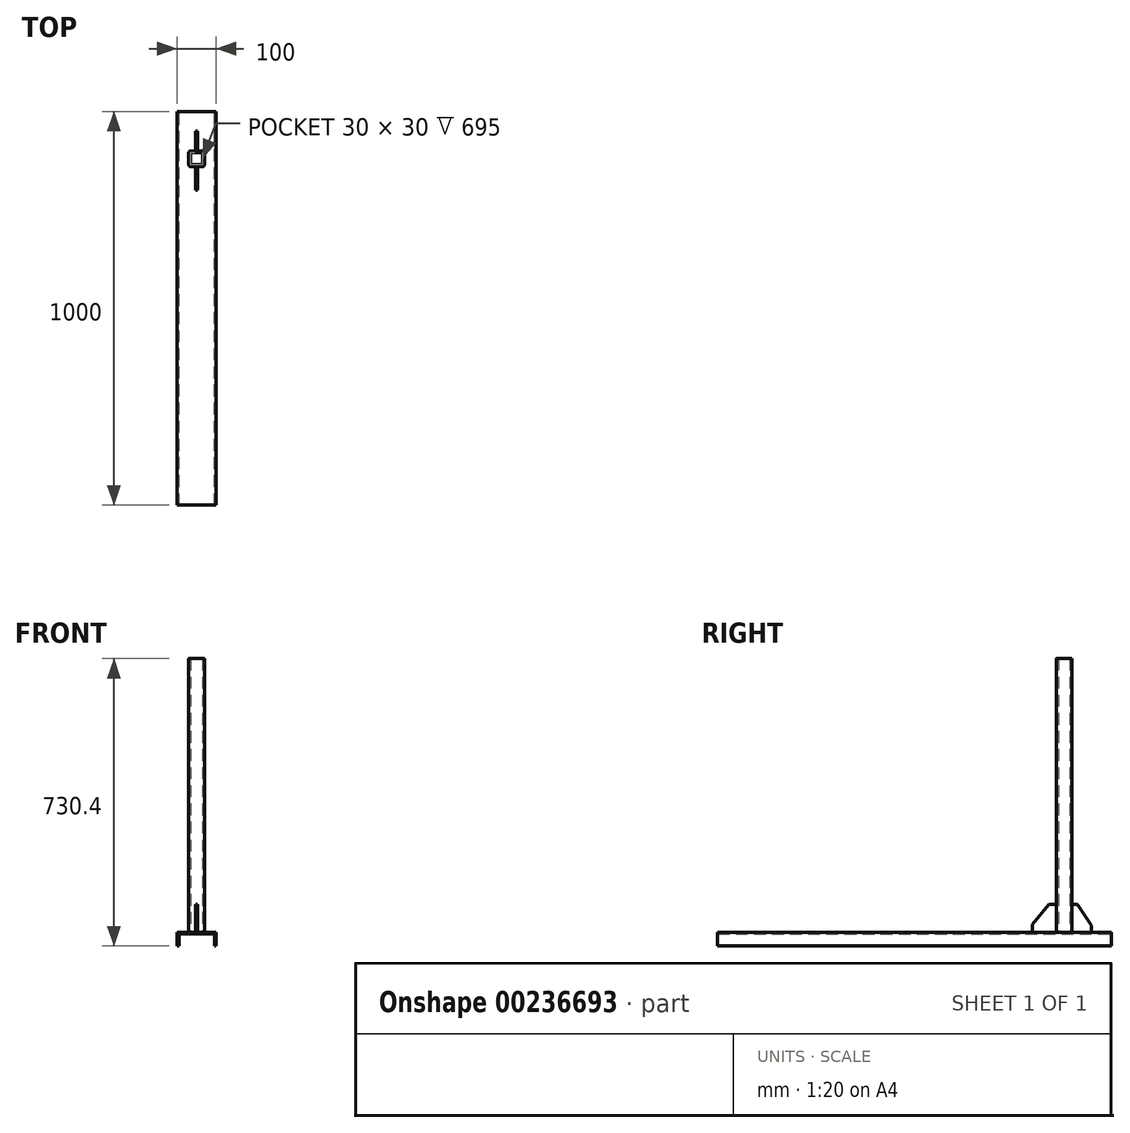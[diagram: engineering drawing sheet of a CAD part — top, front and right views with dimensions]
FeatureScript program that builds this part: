
annotation { "Feature Type Name" : "Feature", "Feature Type Description" : "" }
export const myFeature = defineFeature(function(context is Context, id is Id, definition is map)
    precondition{}
    {
        {
            var Q0;
            Q0=qCreatedBy(makeId("Top.planeOp"),FACE);
            var sketch = newSketch(context, id + "F0", { "sketchPlane" : qUnion([Q0])});
            skLineSegment(sketch, "E0.bottom", {"start": v(5, 0) * mm, "end": v(35, 0) * mm});
            skLineSegment(sketch, "E0.top", {"start": v(5, 40) * mm, "end": v(35, 40) * mm});
            skLineSegment(sketch, "E0.left", {"start": v(0, 5) * mm, "end": v(0, 35) * mm});
            skLineSegment(sketch, "E0.right", {"start": v(40, 5) * mm, "end": v(40, 35) * mm});
            skPoint(sketch, "E1.visualSharp", {"position": v(0, 40) * mm});
            skArc(sketch, "E1.filletArc", {"start": v(5, 40) * mm, "mid": v(1.46, 38.54) * mm, "end": v(0, 35) * mm});
            skPoint(sketch, "E2.visualSharp", {"position": v(0, 0) * mm});
            skArc(sketch, "E2.filletArc", {"start": v(0, 5) * mm, "mid": v(1.46, 1.46) * mm, "end": v(5, 0) * mm});
            skPoint(sketch, "E3.visualSharp", {"position": v(40, 0) * mm});
            skArc(sketch, "E3.filletArc", {"start": v(35, 0) * mm, "mid": v(38.54, 1.46) * mm, "end": v(40, 5) * mm});
            skPoint(sketch, "E4.visualSharp", {"position": v(40, 40) * mm});
            skArc(sketch, "E4.filletArc", {"start": v(40, 35) * mm, "mid": v(38.54, 38.54) * mm, "end": v(35, 40) * mm});
            skLineSegment(sketch, "E5.bottom", {"start": v(35, 5) * mm, "end": v(5, 5) * mm});
            skLineSegment(sketch, "E5.top", {"start": v(35, 35) * mm, "end": v(5, 35) * mm});
            skLineSegment(sketch, "E5.left", {"start": v(35, 5) * mm, "end": v(35, 35) * mm});
            skLineSegment(sketch, "E5.right", {"start": v(5, 5) * mm, "end": v(5, 35) * mm});
            skPoint(sketch, "E5.middle", {"position": v(20, 20) * mm});
            skPoint(sketch, "E5.middle.positionSnap0", {"position": v(0, 20) * mm});
            skPoint(sketch, "E5.middle.positionSnap1", {"position": v(20, 40) * mm});
            skPoint(sketch, "E5.centerSnap0", {"position": v(0, 20) * mm});
            skPoint(sketch, "E5.centerSnap1", {"position": v(20, 40) * mm});
            skSolve(sketch);
        }
        {
            var Q0;
            Q0 = qSketchRegion(id + "F0", true);
            extrude(context, id + "F1", {"entities" : qUnion([Q0]), "depth" : 700 * mm, "offsetDistance" : 25 * mm});
        }
        {
            var Q0;
            Q0=qCreatedBy(makeId("Top.planeOp"),FACE);
            var sketch = newSketch(context, id + "F2", { "sketchPlane" : qUnion([Q0])});
            skLineSegment(sketch, "E6.bottom", {"start": v(70, 140) * mm, "end": v(-30, 140) * mm});
            skLineSegment(sketch, "E6.top", {"start": v(70, -860) * mm, "end": v(-30, -860) * mm});
            skLineSegment(sketch, "E6.left", {"start": v(70, 140) * mm, "end": v(70, -860) * mm});
            skLineSegment(sketch, "E6.right", {"start": v(-30, 140) * mm, "end": v(-30, -860) * mm});
            skPoint(sketch, "E6.middle", {"position": v(20, -360) * mm});
            skSolve(sketch);
        }
        {
            var Q0;
            Q0 = qSketchRegion(id + "F2", true);
            var Q1;
            Q1=makeQuery(id+"F2.imprint","IMPRINT",FACE,{"disambiguationData":[TD([[makeQuery(id+"F2.imprint","IMPRINT",EDGE,{"derivedFrom":sQuery(id+"F2.wireOp",EDGE,"E6.bottom")}),1.0]])]});
            extrude(context, id + "F3", {"entities" : qUnion([Q0, Q1]), "operationType" : NewBodyOperationType.ADD, "depth" : 5 * mm, "offsetDistance" : 25 * mm});
        }
        {
            var Q0;
            Q0=makeQuery(id+"F3.opExtrude","SWEPT_FACE",FACE,{"disambiguationData":[OSD([sQuery(id+"F2.wireOp",EDGE,"E6.bottom")])]});
            var sketch = newSketch(context, id + "F4", { "sketchPlane" : qUnion([Q0])});
            skLineSegment(sketch, "E7.bottom", {"start": v(-70, 0) * mm, "end": v(-65.22, 0) * mm});
            skLineSegment(sketch, "E7.top", {"start": v(-70, -30.4) * mm, "end": v(-65.22, -30.4) * mm});
            skLineSegment(sketch, "E7.left", {"start": v(-70, 0) * mm, "end": v(-70, -30.4) * mm});
            skLineSegment(sketch, "E7.right", {"start": v(-65.22, 0) * mm, "end": v(-65.22, -30.4) * mm});
            skLineSegment(sketch, "E8.bottom", {"start": v(30, 0) * mm, "end": v(24.47, 0) * mm});
            skLineSegment(sketch, "E8.top", {"start": v(30, -30.4) * mm, "end": v(24.47, -30.4) * mm});
            skLineSegment(sketch, "E8.left", {"start": v(30, 0) * mm, "end": v(30, -30.4) * mm});
            skLineSegment(sketch, "E8.right", {"start": v(24.47, 0) * mm, "end": v(24.47, -30.4) * mm});
            skSolve(sketch);
        }
        {
            var Q0;
            Q0 = qSketchRegion(id + "F4", true);
            extrude(context, id + "F5", {"entities" : qUnion([Q0]), "operationType" : NewBodyOperationType.ADD, "oppositeDirection" : true, "depth" : 1000 * mm, "offsetDistance" : 25 * mm});
        }
        {
            var Q0;
            Q0=makeQuery(id+"F1.opExtrude","SWEPT_FACE",FACE,{"disambiguationData":[OSD([sQuery(id+"F0.wireOp",EDGE,"E0.top")])]});
            var sketch = newSketch(context, id + "F6", { "sketchPlane" : qUnion([Q0])});
            skLineSegment(sketch, "E9", {"start": v(-17, 75) * mm, "end": v(-17, 5) * mm});
            skLineSegment(sketch, "E10", {"start": v(-17, 5) * mm, "end": v(-20, 5) * mm});
            skLineSegment(sketch, "E11", {"start": v(-20, 5) * mm, "end": v(-17, 5) * mm});
            skLineSegment(sketch, "E12", {"start": v(-22, 5) * mm, "end": v(-22, 75) * mm});
            skLineSegment(sketch, "E13", {"start": v(-22, 75) * mm, "end": v(-17, 75) * mm});
            skLineSegment(sketch, "E14", {"start": v(-22, 5) * mm, "end": v(-17, 5) * mm});
            skSolve(sketch);
        }
        {
            var Q0;
            Q0 = qSketchRegion(id + "F6", true);
            extrude(context, id + "F7", {"entities" : qUnion([Q0]), "operationType" : NewBodyOperationType.ADD, "depth" : 50 * mm, "offsetDistance" : 25 * mm});
        }
        {
            var Q0;
            Q0=makeQuery(id+"F7.opExtrude","SWEPT_FACE",FACE,{"disambiguationData":[OSD([sQuery(id+"F6.wireOp",EDGE,"E9")])]});
            var sketch = newSketch(context, id + "F8", { "sketchPlane" : qUnion([Q0])});
            skLineSegment(sketch, "E15", {"start": v(-54.04, 75) * mm, "end": v(-90, 21.73) * mm});
            skLineSegment(sketch, "E16", {"start": v(-90, 21.73) * mm, "end": v(-94.03, 21.73) * mm});
            skLineSegment(sketch, "E17", {"start": v(-94.03, 21.73) * mm, "end": v(-94.03, 81.2) * mm});
            skLineSegment(sketch, "E18", {"start": v(-94.03, 81.2) * mm, "end": v(-54.04, 81.2) * mm});
            skLineSegment(sketch, "E19", {"start": v(-54.04, 81.2) * mm, "end": v(-54.04, 75) * mm});
            skSolve(sketch);
        }
        {
            var Q0;
            Q0 = qSketchRegion(id + "F8", true);
            extrude(context, id + "F9", {"entities" : qUnion([Q0]), "operationType" : NewBodyOperationType.REMOVE, "oppositeDirection" : true, "depth" : 25 * mm, "offsetDistance" : 25 * mm});
        }
        {
            var Q0;
            Q0=makeQuery(id+"F1.opExtrude","SWEPT_FACE",FACE,{"disambiguationData":[OSD([sQuery(id+"F0.wireOp",EDGE,"E0.bottom")])]});
            var sketch = newSketch(context, id + "F10", { "sketchPlane" : qUnion([Q0])});
            skLineSegment(sketch, "E20.bottom", {"start": v(17.5, 5) * mm, "end": v(22.5, 5) * mm});
            skLineSegment(sketch, "E20.top", {"start": v(17.5, 75) * mm, "end": v(22.5, 75) * mm});
            skLineSegment(sketch, "E20.left", {"start": v(17.5, 5) * mm, "end": v(17.5, 75) * mm});
            skLineSegment(sketch, "E20.right", {"start": v(22.5, 5) * mm, "end": v(22.5, 75) * mm});
            skSolve(sketch);
        }
        {
            var Q0;
            Q0 = qSketchRegion(id + "F10", true);
            extrude(context, id + "F11", {"entities" : qUnion([Q0]), "operationType" : NewBodyOperationType.ADD, "depth" : 60 * mm, "offsetDistance" : 25 * mm});
        }
        {
            var Q0;
            Q0=makeQuery(id+"F11.opExtrude","SWEPT_FACE",FACE,{"disambiguationData":[OSD([sQuery(id+"F10.wireOp",EDGE,"E20.right")])]});
            var sketch = newSketch(context, id + "F12", { "sketchPlane" : qUnion([Q0])});
            skLineSegment(sketch, "E21", {"start": v(-14, 80) * mm, "end": v(-64, 20.41) * mm});
            skLineSegment(sketch, "E22", {"start": v(-64, 20.41) * mm, "end": v(-64, 80) * mm});
            skLineSegment(sketch, "E23", {"start": v(-64, 80) * mm, "end": v(-14, 80) * mm});
            skSolve(sketch);
        }
        {
            var Q0;
            {var subQ0=sQuery(id+"F12.wireOp",EDGE,"E21");var subQ1=sQuery(id+"F10.wireOp",EDGE,"E20.right");var subQ4=makeQuery(id+"F11.opExtrude","CAP_EDGE",EDGE,{"disambiguationData":[OSD([subQ1])],"isStart":false});var subQ5=makeQuery(id+"F12.imprint","INTERSECT",VERTEX,{"derivedFrom":[subQ4,subQ0]});Q0=makeQuery(id+"F12.imprint","IMPRINT",FACE,{"disambiguationData":[TD([[makeQuery(id+"F12.imprint","IMPRINT",EDGE,{"disambiguationData":[TD([[subQ5,1.0]])],"derivedFrom":subQ0}),-1.0]])]});}
            extrude(context, id + "F13", {"entities" : qUnion([Q0]), "operationType" : NewBodyOperationType.REMOVE, "oppositeDirection" : true, "depth" : 25 * mm, "offsetDistance" : 25 * mm});
        }
    });
